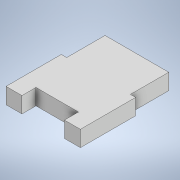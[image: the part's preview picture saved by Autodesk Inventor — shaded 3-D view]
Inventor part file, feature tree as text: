
AUTODESK INVENTOR PART (.ipt)
format: ipt  version: 2021 (Build 250183000, 183)  size: 103,936 bytes
history: native  units: mm
features: extrude x1, sketch x1
ambient origin geometry x8: Origin, YZ Plane, XZ Plane, XY Plane, X Axis, Y Axis, Z Axis, Center Point
bodies: Solid1 (feature_tree)
feature tree (2):
  extrude  "Extrusion1"  Depth=13.2mm
  sketch  "Sketch1"  dims[d0=15.0mm d1=13.2mm d2=40.0mm d3=15.0mm d4=52.0mm d5=5.1mm d6=36.1mm d7=60.0mm d8=15.0mm d9=0.0mm]
